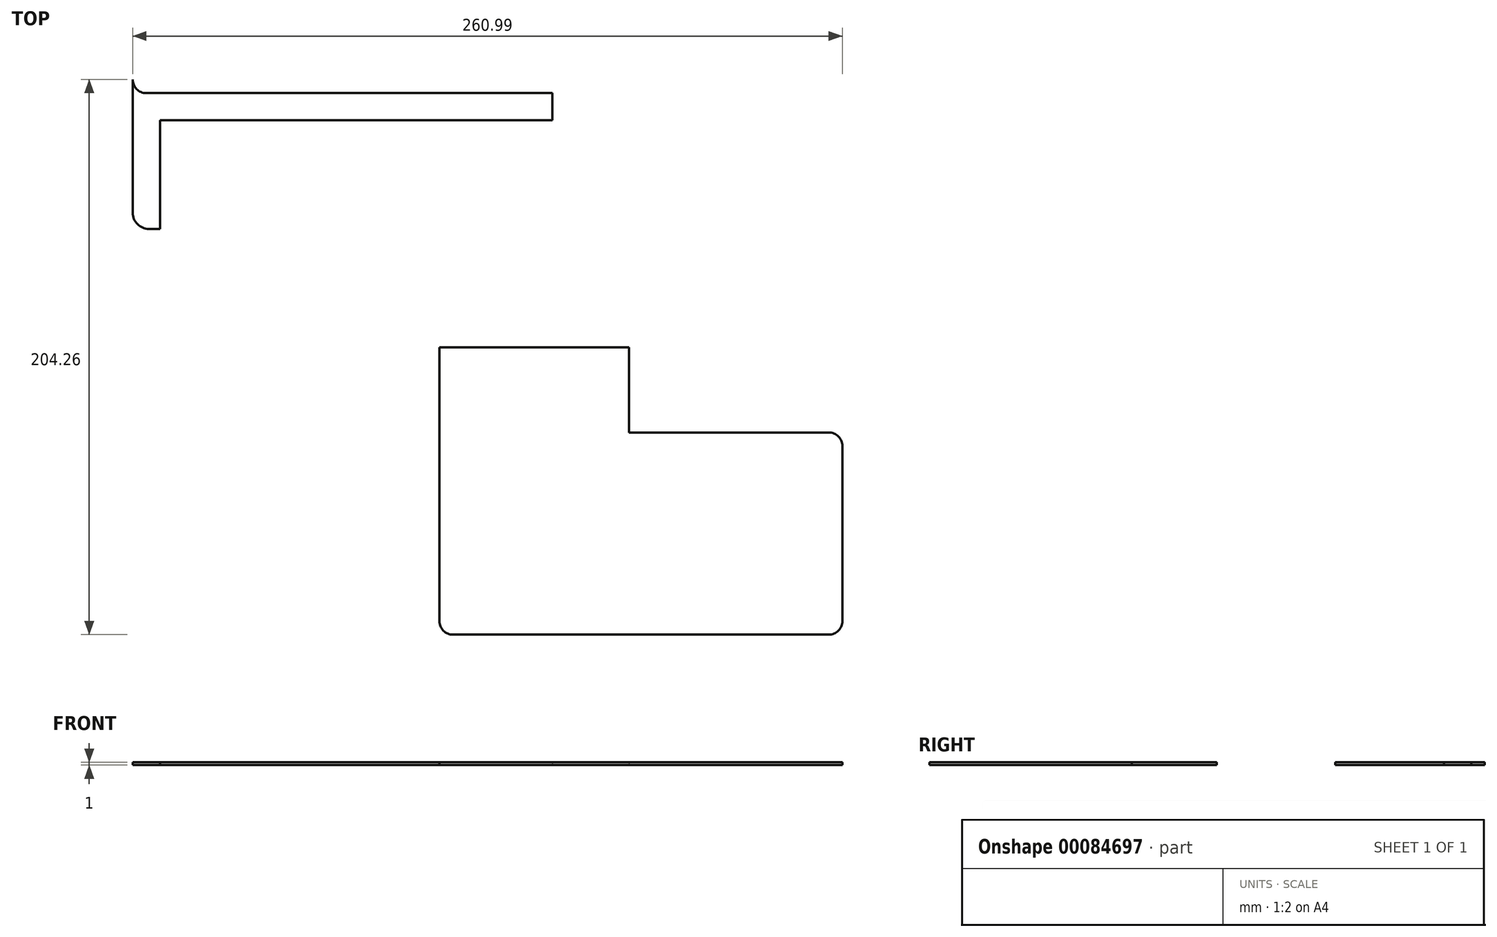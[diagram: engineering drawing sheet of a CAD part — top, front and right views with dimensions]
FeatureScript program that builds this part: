
annotation { "Feature Type Name" : "Feature", "Feature Type Description" : "" }
export const myFeature = defineFeature(function(context is Context, id is Id, definition is map)
    precondition{}
    {
        {
            var Q0;
            Q0=qCreatedBy(makeId("Top.planeOp"),FACE);
            var sketch = newSketch(context, id + "F0", { "sketchPlane" : qUnion([Q0])});
            skLineSegment(sketch, "E0", {"start": v(-154.3, 10) * mm, "end": v(0, 10) * mm});
            skLineSegment(sketch, "E1", {"start": v(28.2, -114.86) * mm, "end": v(106.7, -114.86) * mm});
            skLineSegment(sketch, "E2", {"start": v(106.7, -114.86) * mm, "end": v(106.7, -189.26) * mm});
            skLineSegment(sketch, "E3", {"start": v(106.7, -189.26) * mm, "end": v(-41.5, -189.26) * mm});
            skLineSegment(sketch, "E4", {"start": v(-41.5, -189.26) * mm, "end": v(-41.5, -83.56) * mm});
            skLineSegment(sketch, "E5", {"start": v(-154.3, 0) * mm, "end": v(-154.3, 10) * mm});
            skLineSegment(sketch, "E6", {"start": v(-154.3, 0) * mm, "end": v(0, 0) * mm});
            skLineSegment(sketch, "E7", {"start": v(0, 0) * mm, "end": v(0, 10) * mm});
            skLineSegment(sketch, "E8", {"start": v(-41.5, -83.56) * mm, "end": v(28.2, -83.56) * mm});
            skLineSegment(sketch, "E9", {"start": v(28.2, -83.56) * mm, "end": v(28.2, -114.86) * mm});
            skLineSegment(sketch, "E10", {"start": v(-154.3, 10) * mm, "end": v(-154.3, 15) * mm});
            skArc(sketch, "E11", {"start": v(-154.3, 15) * mm, "mid": v(-152.84, 11.46) * mm, "end": v(-149.3, 10) * mm});
            skLineSegment(sketch, "E12", {"start": v(-154.3, 0) * mm, "end": v(-154.3, -40) * mm});
            skLineSegment(sketch, "E13", {"start": v(-154.3, -40) * mm, "end": v(-144.3, -40) * mm});
            skLineSegment(sketch, "E14", {"start": v(-144.3, -40) * mm, "end": v(-144.3, 0) * mm});
            skSolve(sketch);
        }
        {
            var Q0;
            Q0=makeQuery(id+"F0.imprint","IMPRINT",FACE,{"disambiguationData":[TD([[makeQuery(id+"F0.imprint","IMPRINT",EDGE,{"derivedFrom":sQuery(id+"F0.wireOp",EDGE,"E0")}),-1.0]])]});
            var Q1;
            {var subQ0=sQuery(id+"F0.wireOp",EDGE,"E10");Q1=makeQuery(id+"F0.imprint","IMPRINT",FACE,{"disambiguationData":[TD([[makeQuery(id+"F0.imprint","IMPRINT",EDGE,{"derivedFrom":subQ0}),-1.0]])]});}
            var Q2;
            {var subQ0=sQuery(id+"F0.wireOp",EDGE,"E12");Q2=makeQuery(id+"F0.imprint","IMPRINT",FACE,{"disambiguationData":[TD([[makeQuery(id+"F0.imprint","IMPRINT",EDGE,{"derivedFrom":subQ0}),1.0]])]});}
            extrude(context, id + "F1", {"entities" : qUnion([Q0, Q1, Q2]), "depth" : 1 * mm});
        }
        {
            var Q0;
            Q0=makeQuery(id+"F0.imprint","IMPRINT",FACE,{"disambiguationData":[TD([[makeQuery(id+"F0.imprint","IMPRINT",EDGE,{"derivedFrom":sQuery(id+"F0.wireOp",EDGE,"E1")}),-1.0]])]});
            extrude(context, id + "F2", {"entities" : qUnion([Q0]), "depth" : 1 * mm});
        }
        {
            var Q0;
            Q0=makeQuery(id+"F2.opExtrude","SWEPT_EDGE",EDGE,{"disambiguationData":[OSD([sQuery(id+"F0.wireOp",EDGE,"E3"),sQuery(id+"F0.wireOp",EDGE,"E4")])]});
            var Q1;
            Q1=makeQuery(id+"F2.opExtrude","SWEPT_EDGE",EDGE,{"disambiguationData":[OSD([sQuery(id+"F0.wireOp",EDGE,"E2"),sQuery(id+"F0.wireOp",EDGE,"E3")])]});
            var Q2;
            Q2=makeQuery(id+"F2.opExtrude","SWEPT_EDGE",EDGE,{"disambiguationData":[OSD([sQuery(id+"F0.wireOp",EDGE,"E1"),sQuery(id+"F0.wireOp",EDGE,"E2")])]});
            fillet(context, id + "F3", {"entities" : qUnion([Q0, Q1, Q2]), "radius" : 5 * mm, "tangentPropagation" : true, "allowEdgeOverflow" : false});
        }
        {
            var Q0;
            Q0=makeQuery(id+"F1.opExtrude","SWEPT_EDGE",EDGE,{"disambiguationData":[OSD([sQuery(id+"F0.wireOp",EDGE,"E12"),sQuery(id+"F0.wireOp",EDGE,"E13")])]});
            fillet(context, id + "F4", {"entities" : qUnion([Q0]), "radius" : 6 * mm, "tangentPropagation" : true, "allowEdgeOverflow" : false});
        }
    });
